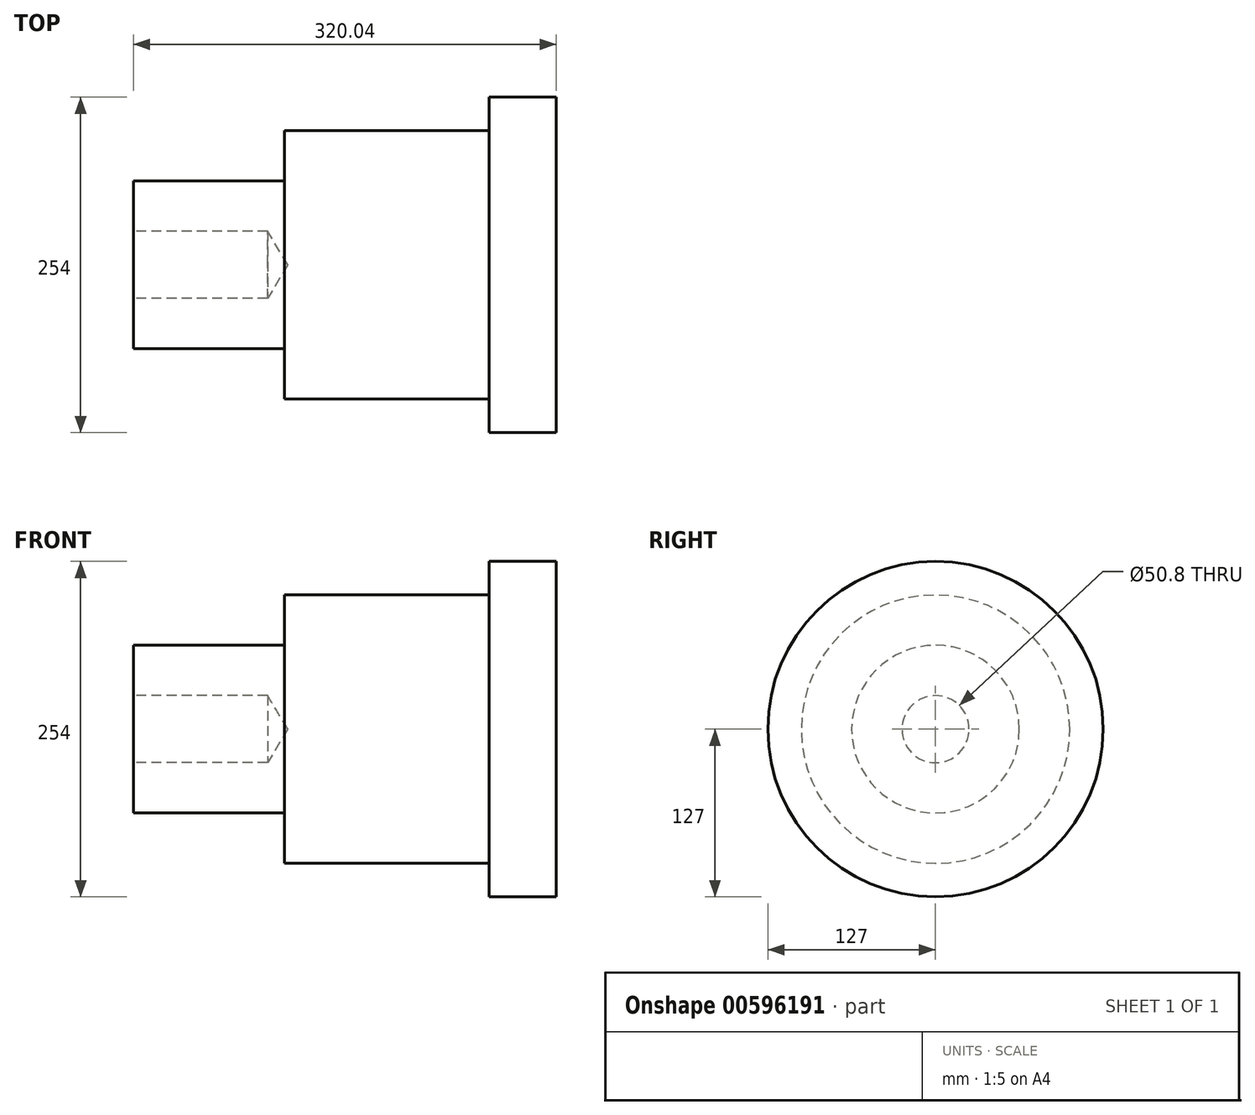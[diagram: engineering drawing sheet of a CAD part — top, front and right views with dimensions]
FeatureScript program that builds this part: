
annotation { "Feature Type Name" : "Feature", "Feature Type Description" : "" }
export const myFeature = defineFeature(function(context is Context, id is Id, definition is map)
    precondition{}
    {
        {
            var Q0;
            Q0=qCreatedBy(makeId("Front.planeOp"),FACE);
            var sketch = newSketch(context, id + "F0", { "sketchPlane" : qUnion([Q0])});
            skLineSegment(sketch, "E0", {"start": v(0, 0) * mm, "end": v(0, 127) * mm});
            skLineSegment(sketch, "E1", {"start": v(0, 127) * mm, "end": v(-50.8, 127) * mm});
            skLineSegment(sketch, "E2", {"start": v(-50.8, 127) * mm, "end": v(-50.8, 0) * mm});
            skLineSegment(sketch, "E3", {"start": v(-50.8, 0) * mm, "end": v(-50.8, 101.6) * mm});
            skLineSegment(sketch, "E4", {"start": v(-50.8, 101.6) * mm, "end": v(-205.74, 101.6) * mm});
            skLineSegment(sketch, "E5", {"start": v(-205.74, 101.6) * mm, "end": v(-205.74, 0) * mm});
            skLineSegment(sketch, "E6", {"start": v(-205.74, 0) * mm, "end": v(-205.74, 63.5) * mm});
            skPoint(sketch, "E6.endSnap0", {"position": v(0, 63.5) * mm});
            skPoint(sketch, "E6.endSnap1", {"position": v(-205.74, 50.8) * mm});
            skLineSegment(sketch, "E7", {"start": v(-205.74, 63.5) * mm, "end": v(-320.04, 63.5) * mm});
            skLineSegment(sketch, "E8", {"start": v(-320.04, 63.5) * mm, "end": v(-320.04, 0) * mm});
            skLineSegment(sketch, "E9", {"start": v(-320.04, 0) * mm, "end": v(-320.04, 22.44) * mm});
            skLineSegment(sketch, "E10", {"start": v(-320.04, 0) * mm, "end": v(0, 0) * mm});
            skSolve(sketch);
        }
        {
            var Q0;
            Q0 = qSketchRegion(id + "F0", true);
            var Q1;
            Q1=sQuery(id+"F0.wireOp",EDGE,"E10");
            revolve(context, id + "F1", {"entities" : qUnion([Q0]), "axis" : qUnion([Q1]), "revolveType" : RevolveType.FULL});
        }
        {
            var Q0;
            Q0=makeQuery(id+"F1.opRevolve","SWEPT_FACE",FACE,{"disambiguationData":[OSD([sQuery(id+"F0.wireOp",EDGE,"E8"),sQuery(id+"F0.wireOp",EDGE,"E9")])]});
            var sketch = newSketch(context, id + "F2", { "sketchPlane" : qUnion([Q0])});
            skPoint(sketch, "E11", {"position": v(0, 0) * mm});
            skSolve(sketch);
        }
        {
            var Q0;
            Q0=sQuery(id+"F2.wireOp",VERTEX,"E11");
            var Q1;
            Q1=makeQuery(id+"F1.opRevolve","SWEPT_BODY",BODY,{"disambiguationData":[OSD([sQuery(id+"F0.wireOp",EDGE,"E0"),sQuery(id+"F0.wireOp",EDGE,"E1"),sQuery(id+"F0.wireOp",EDGE,"E2"),sQuery(id+"F0.wireOp",EDGE,"E4"),sQuery(id+"F0.wireOp",EDGE,"E5"),sQuery(id+"F0.wireOp",EDGE,"E7"),sQuery(id+"F0.wireOp",EDGE,"E8"),sQuery(id+"F0.wireOp",EDGE,"E9"),sQuery(id+"F0.wireOp",EDGE,"E10")])]});
            hole(context, id + "F3", {"style" : HoleStyle.SIMPLE, "endStyle" : HoleEndStyle.BLIND, "holeDiameter" : 50.8 * mm, "majorDiameter" : 6.35 * mm, "holeDepth" : 101.6 * mm, "isTappedThrough" : true, "tappedDepth" : 12.7 * mm, "tapClearance" : 3, "locations" : qUnion([Q0]), "scope" : qUnion([Q1])});
        }
    });
